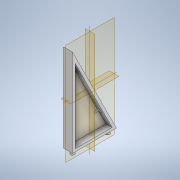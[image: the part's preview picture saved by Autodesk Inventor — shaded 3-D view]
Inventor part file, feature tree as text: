
AUTODESK INVENTOR PART (.ipt)
format: ipt  version: 2022.4 (Build 264492010, 492A)  size: 147,456 bytes
history: native  units: mm
features: extrude x4, sketch x4, mirror x1
ambient origin geometry x8: Origin, YZ Plane, XZ Plane, XY Plane, X Axis, Y Axis, Z Axis, Center Point
bodies: Solid1 (feature_tree)
feature tree (9):
  extrude  "Extrusion1"  Depth=100.0mm
  extrude  "Extrusion2"  Depth=3.0mm
  extrude  "Extrusion3"  Depth=5.0mm
  extrude  "Extrusion4"  Depth=10.0mm
  mirror  "Mirror1"
  sketch  "Sketch2"  dims[d0=50.0mm d1=100.0mm]
  sketch  "Sketch4"  dims[d2=10.0mm d3=0.0mm d8=3.0mm]
  sketch  "Sketch5"  dims[d9=7.0mm d10=0.0mm d11=5.0mm]
  sketch  "Sketch8"  dims[d12=5.0mm d13=20.0mm d15=40.0mm d16=10.0mm d18=10.0mm d20=5.0mm d21=0.0mm d31=111.803399mm d32=5.0mm d34=30.0mm d35=7.0mm d36=0.0mm]
